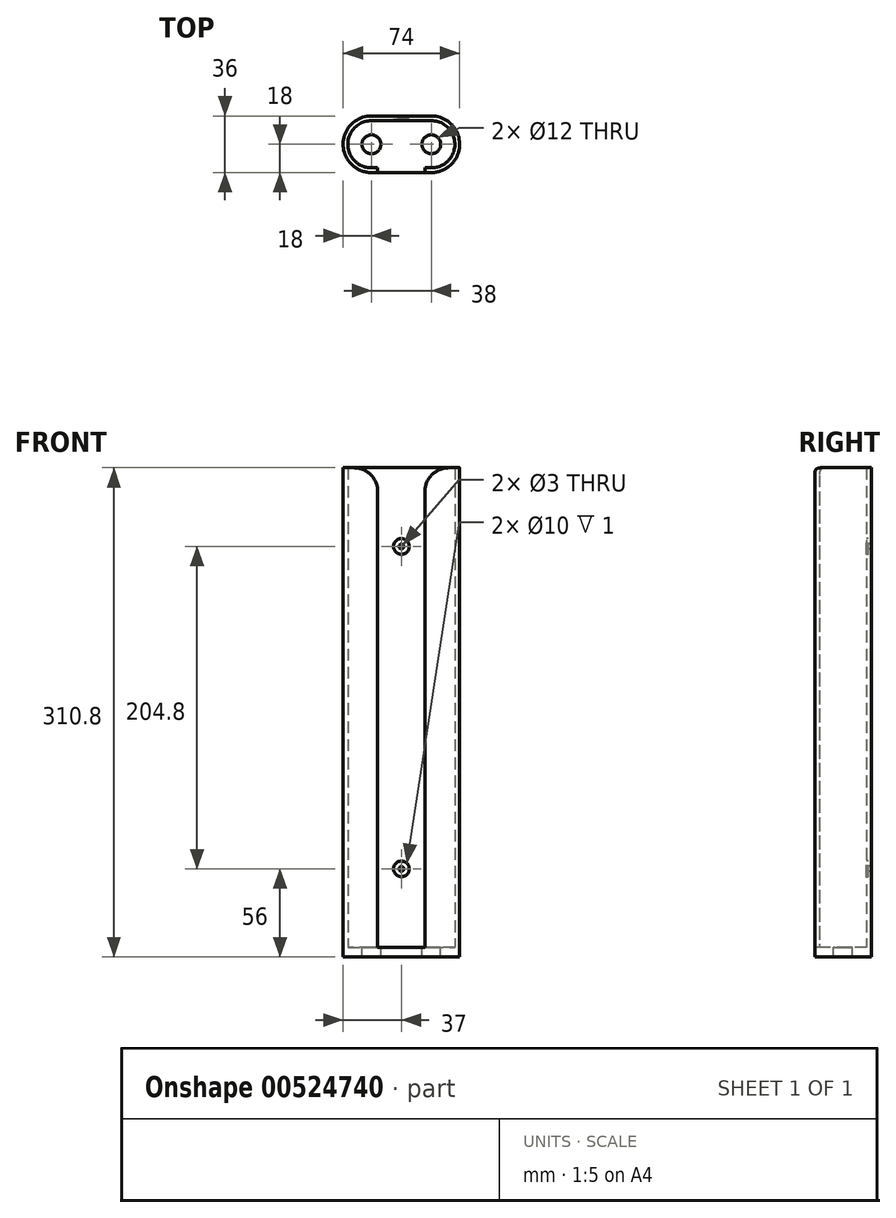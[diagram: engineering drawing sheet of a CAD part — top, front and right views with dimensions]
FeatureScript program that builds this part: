
annotation { "Feature Type Name" : "Feature", "Feature Type Description" : "" }
export const myFeature = defineFeature(function(context is Context, id is Id, definition is map)
    precondition{}
    {
        {
            var Q0;
            Q0=qCreatedBy(makeId("Top.planeOp"),FACE);
            var sketch = newSketch(context, id + "F0", { "sketchPlane" : qUnion([Q0])});
            skLineSegment(sketch, "E0", {"start": v(0, 36.92) * mm, "end": v(0, -40.78) * mm, "construction": true});
            skLineSegment(sketch, "E1", {"start": v(48.74, 0) * mm, "end": v(-59.01, 0) * mm, "construction": true});
            skArc(sketch, "E2", {"start": v(-19, 15) * mm, "mid": v(-34, -0.02) * mm, "end": v(-18.95, -15) * mm});
            skLineSegment(sketch, "E3", {"start": v(-19, 0) * mm, "end": v(-19, 37.51) * mm, "construction": true});
            skLineSegment(sketch, "E4", {"start": v(-19, 15) * mm, "end": v(0, 15) * mm});
            skLineSegment(sketch, "E5", {"start": v(-19.05, -15) * mm, "end": v(-15, -15) * mm});
            skPoint(sketch, "E6.orphan", {"position": v(0, -15) * mm});
            skPoint(sketch, "E7.MirrorCS.end.orphan", {"position": v(0, 15) * mm});
            skLineSegment(sketch, "E8", {"start": v(-15, -15) * mm, "end": v(-15, -18) * mm});
            skLineSegment(sketch, "E9.0", {"start": v(-19, 18) * mm, "end": v(0, 18) * mm});
            skArc(sketch, "E9.1", {"start": v(-19, 18) * mm, "mid": v(-37, 0) * mm, "end": v(-19, -18) * mm});
            skLineSegment(sketch, "E10", {"start": v(-19, -18) * mm, "end": v(-15, -18) * mm});
            skLineSegment(sketch, "E11.MirrorCS", {"start": v(15, -15) * mm, "end": v(15, -18) * mm});
            skLineSegment(sketch, "E12.MirrorCS", {"start": v(19, 15) * mm, "end": v(0, 15) * mm});
            skArc(sketch, "E13.MirrorCS", {"start": v(19, 15) * mm, "mid": v(34, -0.02) * mm, "end": v(18.95, -15) * mm});
            skLineSegment(sketch, "E14.MirrorCS", {"start": v(19, -18) * mm, "end": v(15, -18) * mm});
            skArc(sketch, "E15.MirrorCS", {"start": v(19, 18) * mm, "mid": v(37, 0) * mm, "end": v(19, -18) * mm});
            skLineSegment(sketch, "E16.MirrorCS", {"start": v(19, 18) * mm, "end": v(0, 18) * mm});
            skLineSegment(sketch, "E17.MirrorCS", {"start": v(19.05, -15) * mm, "end": v(15, -15) * mm});
            skSolve(sketch);
        }
        {
            var Q0;
            {var subQ2=sQuery(id+"F0.wireOp",EDGE,"E2");Q0=makeQuery(id+"F0.imprint","IMPRINT",FACE,{"disambiguationData":[TD([[makeQuery(id+"F0.imprint","IMPRINT",EDGE,{"derivedFrom":subQ2}),-1.0]])]});}
            extrude(context, id + "F1", {"entities" : qUnion([Q0]), "depth" : 304.8 * mm, "offsetDistance" : 25.4 * mm});
        }
        {
            var Q0;
            Q0=makeQuery(id+"F1.opExtrude","CAP_EDGE",EDGE,{"disambiguationData":[OSD([sQuery(id+"F0.wireOp",EDGE,"E8")])],"isStart":false});
            var Q1;
            Q1=makeQuery(id+"F1.opExtrude","CAP_EDGE",EDGE,{"disambiguationData":[OSD([sQuery(id+"F0.wireOp",EDGE,"E11.MirrorCS")])],"isStart":false});
            fillet(context, id + "F2", {"entities" : qUnion([Q0, Q1]), "radius" : 15 * mm, "tangentPropagation" : true, "allowEdgeOverflow" : false});
        }
        {
            var Q0;
            Q0=makeQuery(id+"F1.opExtrude","SWEPT_FACE",FACE,{"disambiguationData":[OSD([sQuery(id+"F0.wireOp",EDGE,"E4"),sQuery(id+"F0.wireOp",EDGE,"E12.MirrorCS")])]});
            var sketch = newSketch(context, id + "F3", { "sketchPlane" : qUnion([Q0])});
            skLineSegment(sketch, "E18", {"start": v(0, 304.8) * mm, "end": v(0, 0) * mm, "construction": true});
            skPoint(sketch, "E19", {"position": v(0, 254.8) * mm});
            skPoint(sketch, "E20", {"position": v(0, 50) * mm});
            skSolve(sketch);
        }
        {
            var Q0;
            Q0=sQuery(id+"F3.wireOp",VERTEX,"E19");
            var Q1;
            Q1=sQuery(id+"F3.wireOp",VERTEX,"E20");
            var Q2;
            Q2=makeQuery(id+"F1.opExtrude","SWEPT_BODY",BODY,{"disambiguationData":[OSD([sQuery(id+"F0.wireOp",EDGE,"E2"),sQuery(id+"F0.wireOp",EDGE,"E4"),sQuery(id+"F0.wireOp",EDGE,"E5"),sQuery(id+"F0.wireOp",EDGE,"E8"),sQuery(id+"F0.wireOp",EDGE,"E9.0"),sQuery(id+"F0.wireOp",EDGE,"E9.1"),sQuery(id+"F0.wireOp",EDGE,"E10"),sQuery(id+"F0.wireOp",EDGE,"E11.MirrorCS"),sQuery(id+"F0.wireOp",EDGE,"E12.MirrorCS"),sQuery(id+"F0.wireOp",EDGE,"E13.MirrorCS"),sQuery(id+"F0.wireOp",EDGE,"E14.MirrorCS"),sQuery(id+"F0.wireOp",EDGE,"E15.MirrorCS"),sQuery(id+"F0.wireOp",EDGE,"E16.MirrorCS"),sQuery(id+"F0.wireOp",EDGE,"E17.MirrorCS")])]});
            hole(context, id + "F4", {"style" : HoleStyle.C_BORE, "endStyle" : HoleEndStyle.THROUGH, "holeDiameter" : 3 * mm, "cBoreDiameter" : 10 * mm, "cBoreDepth" : 1 * mm, "isTappedThrough" : true, "tappedDepth" : 12 * mm, "tapClearance" : 3, "startFromSketch" : true, "locations" : qUnion([Q0, Q1]), "scope" : qUnion([Q2])});
        }
        {
            var Q0;
            Q0=makeQuery(id+"F1.opExtrude","CAP_FACE",FACE,{"disambiguationData":[OSD([sQuery(id+"F0.wireOp",EDGE,"E2"),sQuery(id+"F0.wireOp",EDGE,"E4"),sQuery(id+"F0.wireOp",EDGE,"E5"),sQuery(id+"F0.wireOp",EDGE,"E8"),sQuery(id+"F0.wireOp",EDGE,"E9.0"),sQuery(id+"F0.wireOp",EDGE,"E9.1"),sQuery(id+"F0.wireOp",EDGE,"E10"),sQuery(id+"F0.wireOp",EDGE,"E11.MirrorCS"),sQuery(id+"F0.wireOp",EDGE,"E12.MirrorCS"),sQuery(id+"F0.wireOp",EDGE,"E13.MirrorCS"),sQuery(id+"F0.wireOp",EDGE,"E14.MirrorCS"),sQuery(id+"F0.wireOp",EDGE,"E15.MirrorCS"),sQuery(id+"F0.wireOp",EDGE,"E16.MirrorCS"),sQuery(id+"F0.wireOp",EDGE,"E17.MirrorCS")])],"isStart":true});
            var sketch = newSketch(context, id + "F5", { "sketchPlane" : qUnion([Q0])});
            skLineSegment(sketch, "E21.0", {"start": v(-19, -18) * mm, "end": v(19, -18) * mm});
            skArc(sketch, "E21.1", {"start": v(-19, -18) * mm, "mid": v(-37, 0) * mm, "end": v(-19, 18) * mm});
            skArc(sketch, "E21.2", {"start": v(19, -18) * mm, "mid": v(37, 0) * mm, "end": v(19, 18) * mm});
            skLineSegment(sketch, "E22", {"start": v(-19, 18) * mm, "end": v(19, 18) * mm});
            skCircle(sketch, "E23", {"center": v(-19, 0) * mm, "radius": 6 * mm});
            skCircle(sketch, "E24", {"center": v(19, 0) * mm, "radius": 6 * mm});
            skSolve(sketch);
        }
        {
            var Q0;
            Q0 = qSketchRegion(id + "F5", true);
            extrude(context, id + "F6", {"entities" : qUnion([Q0]), "operationType" : NewBodyOperationType.ADD, "depth" : 6 * mm, "offsetDistance" : 25 * mm});
        }
    });
